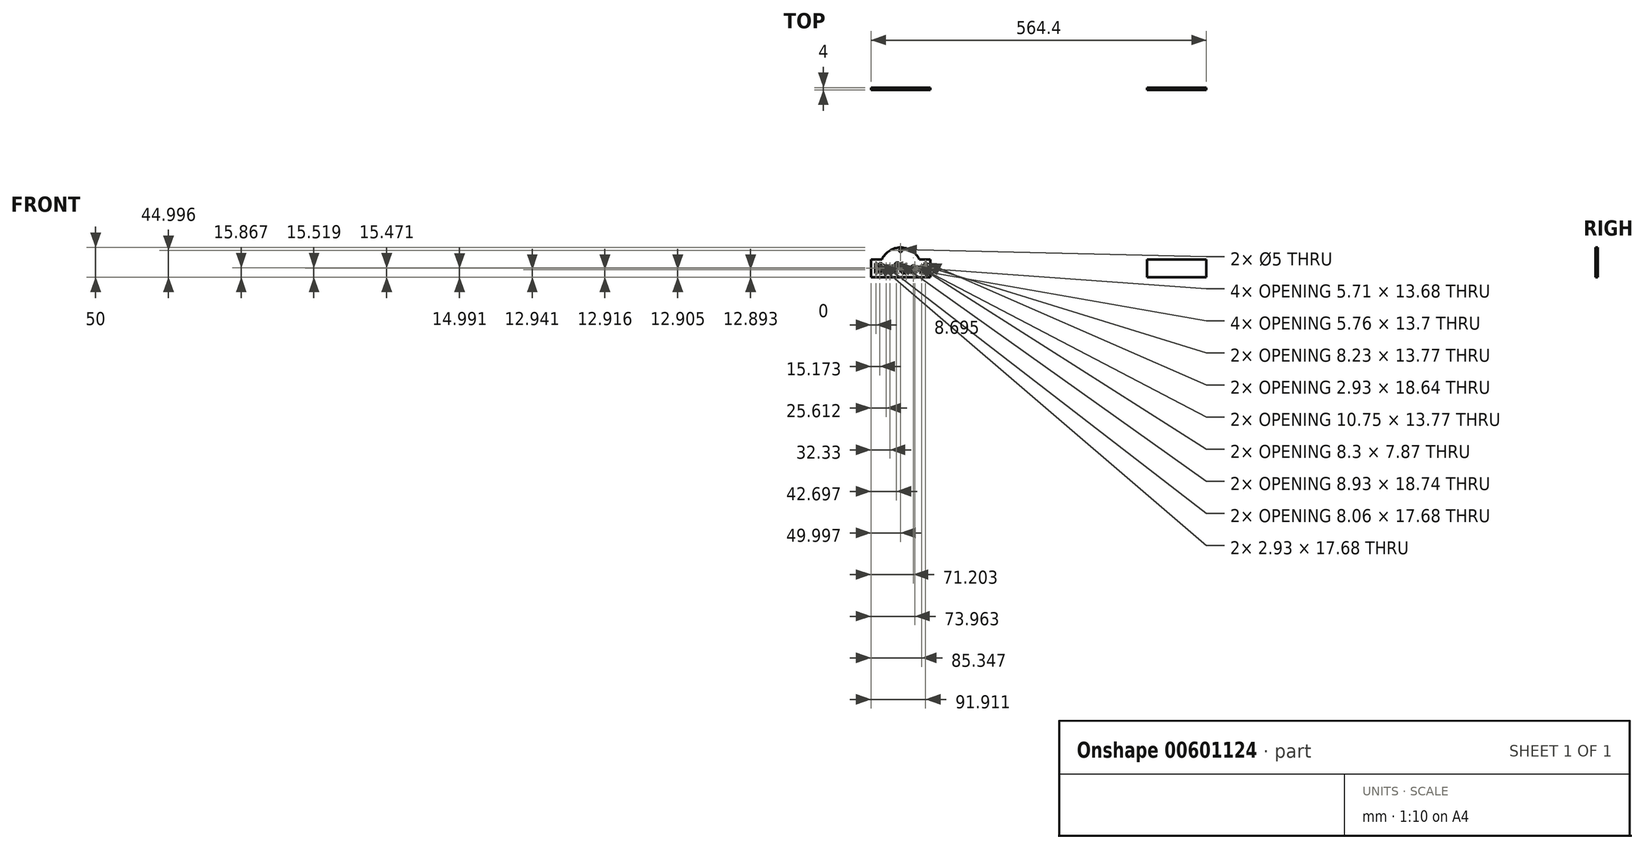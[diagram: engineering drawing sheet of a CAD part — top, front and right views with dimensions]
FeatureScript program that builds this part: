
annotation { "Feature Type Name" : "Feature", "Feature Type Description" : "" }
export const myFeature = defineFeature(function(context is Context, id is Id, definition is map)
    precondition{}
    {
        {
            var Q0;
            Q0=qCreatedBy(makeId("Front.planeOp"),FACE);
            var sketch = newSketch(context, id + "F0", { "sketchPlane" : qUnion([Q0])});
            skLineSegment(sketch, "E0", {"start": v(324.97, 2.68) * mm, "end": v(324.97, -27.32) * mm});
            skLineSegment(sketch, "E1", {"start": v(324.97, -27.32) * mm, "end": v(424.97, -27.32) * mm});
            skLineSegment(sketch, "E2", {"start": v(424.97, -27.32) * mm, "end": v(424.97, 2.68) * mm});
            skLineSegment(sketch, "E3", {"start": v(424.97, 2.68) * mm, "end": v(324.97, 2.68) * mm});
            skArc(sketch, "E4", {"start": v(-57.81, 2.68) * mm, "mid": v(-89.43, 22.68) * mm, "end": v(-121.06, 2.68) * mm});
            skCircle(sketch, "E5", {"center": v(-89.43, 17.68) * mm, "radius": 2.5 * mm});
            skLineSegment(sketch, "E6", {"start": v(-139.43, 2.68) * mm, "end": v(-139.43, -27.32) * mm});
            skLineSegment(sketch, "E7", {"start": v(-39.43, -27.32) * mm, "end": v(-139.43, -27.32) * mm});
            skLineSegment(sketch, "E8", {"start": v(-39.43, -27.32) * mm, "end": v(-39.43, 2.68) * mm});
            skLineSegment(sketch, "E9", {"start": v(-39.43, 2.68) * mm, "end": v(-57.81, 2.68) * mm});
            skPoint(sketch, "E10", {"position": v(-139.43, -12.32) * mm});
            skPoint(sketch, "E11", {"position": v(-89.43, -27.32) * mm});
            skText(sketch, "E12", { "text": "Kofoed\n", "fontName": "AllertaStencil-Regular.ttf"});
            skPoint(sketch, "E13", {"position": v(-44.43, -12.32) * mm});
            skPoint(sketch, "E14", {"position": v(-39.43, -12.32) * mm});
            skLineSegment(sketch, "E15.trimOffspring", {"start": v(-121.06, 2.68) * mm, "end": v(-139.43, 2.68) * mm});
            const initialGuessF0  = {"E12": [-0.13443, -0.02117, 1, 0, 0.01769]};
            skSetInitialGuess(sketch, initialGuessF0);
            skSolve(sketch);
        }
        {
            var Q0;
            Q0=makeQuery(id+"F0.imprint","IMPRINT",FACE,{"disambiguationData":[TD([[makeQuery(id+"F0.imprint","IMPRINT",EDGE,{"derivedFrom":sQuery(id+"F0.wireOp",EDGE,"E4")}),1.0]])]});
            var sketch = newSketch(context, id + "F1", { "sketchPlane" : qUnion([Q0])});
            skSolve(sketch);
        }
        {
            var Q0;
            Q0 = qSketchRegion(id + "F0", true);
            var Q1;
            Q1=makeQuery(id+"F0.imprint","IMPRINT",FACE,{"disambiguationData":[TD([[makeQuery(id+"F0.imprint","IMPRINT",EDGE,{"derivedFrom":sQuery(id+"F0.wireOp",EDGE,"E4")}),1.0]])]});
            var Q2;
            Q2=makeQuery(id+"F0.imprint","IMPRINT",FACE,{"disambiguationData":[TD([[makeQuery(id+"F0.imprint","IMPRINT",EDGE,{"derivedFrom":sQuery(id+"F0.wireOp",EDGE,"E12.sketch_text.stroke-0")}),-1.0]])]});
            var Q3;
            Q3=makeQuery(id+"F0.imprint","IMPRINT",FACE,{"disambiguationData":[TD([[makeQuery(id+"F0.imprint","IMPRINT",EDGE,{"derivedFrom":sQuery(id+"F0.wireOp",EDGE,"E12.sketch_text.stroke-4")}),-1.0]])]});
            var Q4;
            Q4=makeQuery(id+"F0.imprint","IMPRINT",FACE,{"disambiguationData":[TD([[makeQuery(id+"F0.imprint","IMPRINT",EDGE,{"derivedFrom":sQuery(id+"F0.wireOp",EDGE,"E12.sketch_text.stroke-11")}),-1.0]])]});
            var Q5;
            Q5=makeQuery(id+"F0.imprint","IMPRINT",FACE,{"disambiguationData":[TD([[makeQuery(id+"F0.imprint","IMPRINT",EDGE,{"derivedFrom":sQuery(id+"F0.wireOp",EDGE,"E12.sketch_text.stroke-27")}),-1.0]])]});
            var Q6;
            Q6=makeQuery(id+"F0.imprint","IMPRINT",FACE,{"disambiguationData":[TD([[makeQuery(id+"F0.imprint","IMPRINT",EDGE,{"derivedFrom":sQuery(id+"F0.wireOp",EDGE,"E12.sketch_text.stroke-43")}),-1.0]])]});
            var Q7;
            Q7=makeQuery(id+"F0.imprint","IMPRINT",FACE,{"disambiguationData":[TD([[makeQuery(id+"F0.imprint","IMPRINT",EDGE,{"derivedFrom":sQuery(id+"F0.wireOp",EDGE,"E12.sketch_text.stroke-69")}),-1.0]])]});
            var Q8;
            Q8=makeQuery(id+"F0.imprint","IMPRINT",FACE,{"disambiguationData":[TD([[makeQuery(id+"F0.imprint","IMPRINT",EDGE,{"derivedFrom":sQuery(id+"F0.wireOp",EDGE,"E12.sketch_text.stroke-101")}),-1.0]])]});
            var Q9;
            Q9=makeQuery(id+"F0.imprint","IMPRINT",FACE,{"disambiguationData":[TD([[makeQuery(id+"F0.imprint","IMPRINT",EDGE,{"derivedFrom":sQuery(id+"F0.wireOp",EDGE,"E12.sketch_text.stroke-114")}),-1.0]])]});
            var Q10;
            Q10=makeQuery(id+"F0.imprint","IMPRINT",FACE,{"disambiguationData":[TD([[makeQuery(id+"F0.imprint","IMPRINT",EDGE,{"derivedFrom":sQuery(id+"F0.wireOp",EDGE,"E12.sketch_text.stroke-143")}),-1.0]])]});
            var Q11;
            Q11=makeQuery(id+"F1.imprint","IMPRINT",FACE,{"disambiguationData":[TD([[makeQuery(id+"F1.imprint","IMPRINT",EDGE,{"derivedFrom":makeQuery(id+"F0.imprint","IMPRINT",EDGE,{"derivedFrom":sQuery(id+"F0.wireOp",EDGE,"E4")})}),1.0]])]});
            var Q12;
            Q12=makeQuery(id+"F0.imprint","IMPRINT",FACE,{"disambiguationData":[TD([[makeQuery(id+"F0.imprint","IMPRINT",EDGE,{"derivedFrom":sQuery(id+"F0.wireOp",EDGE,"E5")}),1.0]])]});
            var Q13;
            Q13=makeQuery(id+"F0.imprint","IMPRINT",FACE,{"disambiguationData":[TD([[makeQuery(id+"F0.imprint","IMPRINT",EDGE,{"derivedFrom":sQuery(id+"F0.wireOp",EDGE,"E12.sketch_text.stroke-85")}),-1.0]])]});
            var Q14;
            Q14=makeQuery(id+"F0.imprint","IMPRINT",FACE,{"disambiguationData":[TD([[makeQuery(id+"F0.imprint","IMPRINT",EDGE,{"derivedFrom":sQuery(id+"F0.wireOp",EDGE,"E12.sketch_text.stroke-138")}),-1.0]])]});
            var Q15;
            Q15=makeQuery(id+"F1.imprint","IMPRINT",FACE,{"disambiguationData":[TD([[makeQuery(id+"F1.imprint","IMPRINT",EDGE,{"derivedFrom":makeQuery(id+"F0.imprint","IMPRINT",EDGE,{"derivedFrom":sQuery(id+"F0.wireOp",EDGE,"E12.sketch_text.stroke-0")})}),-1.0]])]});
            var Q16;
            Q16=makeQuery(id+"F1.imprint","IMPRINT",FACE,{"disambiguationData":[TD([[makeQuery(id+"F1.imprint","IMPRINT",EDGE,{"derivedFrom":makeQuery(id+"F0.imprint","IMPRINT",EDGE,{"derivedFrom":sQuery(id+"F0.wireOp",EDGE,"E12.sketch_text.stroke-4")})}),-1.0]])]});
            var Q17;
            Q17=makeQuery(id+"F1.imprint","IMPRINT",FACE,{"disambiguationData":[TD([[makeQuery(id+"F1.imprint","IMPRINT",EDGE,{"derivedFrom":makeQuery(id+"F0.imprint","IMPRINT",EDGE,{"derivedFrom":sQuery(id+"F0.wireOp",EDGE,"E12.sketch_text.stroke-11")})}),-1.0]])]});
            var Q18;
            Q18=makeQuery(id+"F1.imprint","IMPRINT",FACE,{"disambiguationData":[TD([[makeQuery(id+"F1.imprint","IMPRINT",EDGE,{"derivedFrom":makeQuery(id+"F0.imprint","IMPRINT",EDGE,{"derivedFrom":sQuery(id+"F0.wireOp",EDGE,"E12.sketch_text.stroke-27")})}),-1.0]])]});
            var Q19;
            Q19=makeQuery(id+"F1.imprint","IMPRINT",FACE,{"disambiguationData":[TD([[makeQuery(id+"F1.imprint","IMPRINT",EDGE,{"derivedFrom":makeQuery(id+"F0.imprint","IMPRINT",EDGE,{"derivedFrom":sQuery(id+"F0.wireOp",EDGE,"E12.sketch_text.stroke-43")})}),-1.0]])]});
            var Q20;
            Q20=makeQuery(id+"F1.imprint","IMPRINT",FACE,{"disambiguationData":[TD([[makeQuery(id+"F1.imprint","IMPRINT",EDGE,{"derivedFrom":makeQuery(id+"F0.imprint","IMPRINT",EDGE,{"derivedFrom":sQuery(id+"F0.wireOp",EDGE,"E12.sketch_text.stroke-69")})}),-1.0]])]});
            var Q21;
            Q21=makeQuery(id+"F1.imprint","IMPRINT",FACE,{"disambiguationData":[TD([[makeQuery(id+"F1.imprint","IMPRINT",EDGE,{"derivedFrom":makeQuery(id+"F0.imprint","IMPRINT",EDGE,{"derivedFrom":sQuery(id+"F0.wireOp",EDGE,"E12.sketch_text.stroke-101")})}),-1.0]])]});
            var Q22;
            Q22=makeQuery(id+"F1.imprint","IMPRINT",FACE,{"disambiguationData":[TD([[makeQuery(id+"F1.imprint","IMPRINT",EDGE,{"derivedFrom":makeQuery(id+"F0.imprint","IMPRINT",EDGE,{"derivedFrom":sQuery(id+"F0.wireOp",EDGE,"E12.sketch_text.stroke-114")})}),-1.0]])]});
            var Q23;
            Q23=makeQuery(id+"F1.imprint","IMPRINT",FACE,{"disambiguationData":[TD([[makeQuery(id+"F1.imprint","IMPRINT",EDGE,{"derivedFrom":makeQuery(id+"F0.imprint","IMPRINT",EDGE,{"derivedFrom":sQuery(id+"F0.wireOp",EDGE,"E12.sketch_text.stroke-143")})}),-1.0]])]});
            var Q24;
            Q24=makeQuery(id+"F1.imprint","IMPRINT",FACE,{"disambiguationData":[TD([[makeQuery(id+"F1.imprint","IMPRINT",EDGE,{"derivedFrom":makeQuery(id+"F0.imprint","IMPRINT",EDGE,{"derivedFrom":sQuery(id+"F0.wireOp",EDGE,"E5")})}),1.0]])]});
            var Q25;
            Q25=makeQuery(id+"F1.imprint","IMPRINT",FACE,{"disambiguationData":[TD([[makeQuery(id+"F1.imprint","IMPRINT",EDGE,{"derivedFrom":makeQuery(id+"F0.imprint","IMPRINT",EDGE,{"derivedFrom":sQuery(id+"F0.wireOp",EDGE,"E12.sketch_text.stroke-85")})}),-1.0]])]});
            var Q26;
            Q26=makeQuery(id+"F1.imprint","IMPRINT",FACE,{"disambiguationData":[TD([[makeQuery(id+"F1.imprint","IMPRINT",EDGE,{"derivedFrom":makeQuery(id+"F0.imprint","IMPRINT",EDGE,{"derivedFrom":sQuery(id+"F0.wireOp",EDGE,"E12.sketch_text.stroke-138")})}),-1.0]])]});
            extrude(context, id + "F2", {"entities" : qUnion([Q0, Q1, Q2, Q3, Q4, Q5, Q6, Q7, Q8, Q9, Q10, Q11, Q12, Q13, Q14, Q15, Q16, Q17, Q18, Q19, Q20, Q21, Q22, Q23, Q24, Q25, Q26]), "depth" : 2 * mm, "offsetDistance" : 25 * mm});
        }
        {
            var Q0;
            Q0 = qSketchRegion(id + "F1", true);
            var Q1;
            Q1 = qSketchRegion(id + "F0", true);
            extrude(context, id + "F3", {"entities" : qUnion([Q0, Q1]), "depth" : 4 * mm, "offsetDistance" : 25 * mm});
        }
    });
